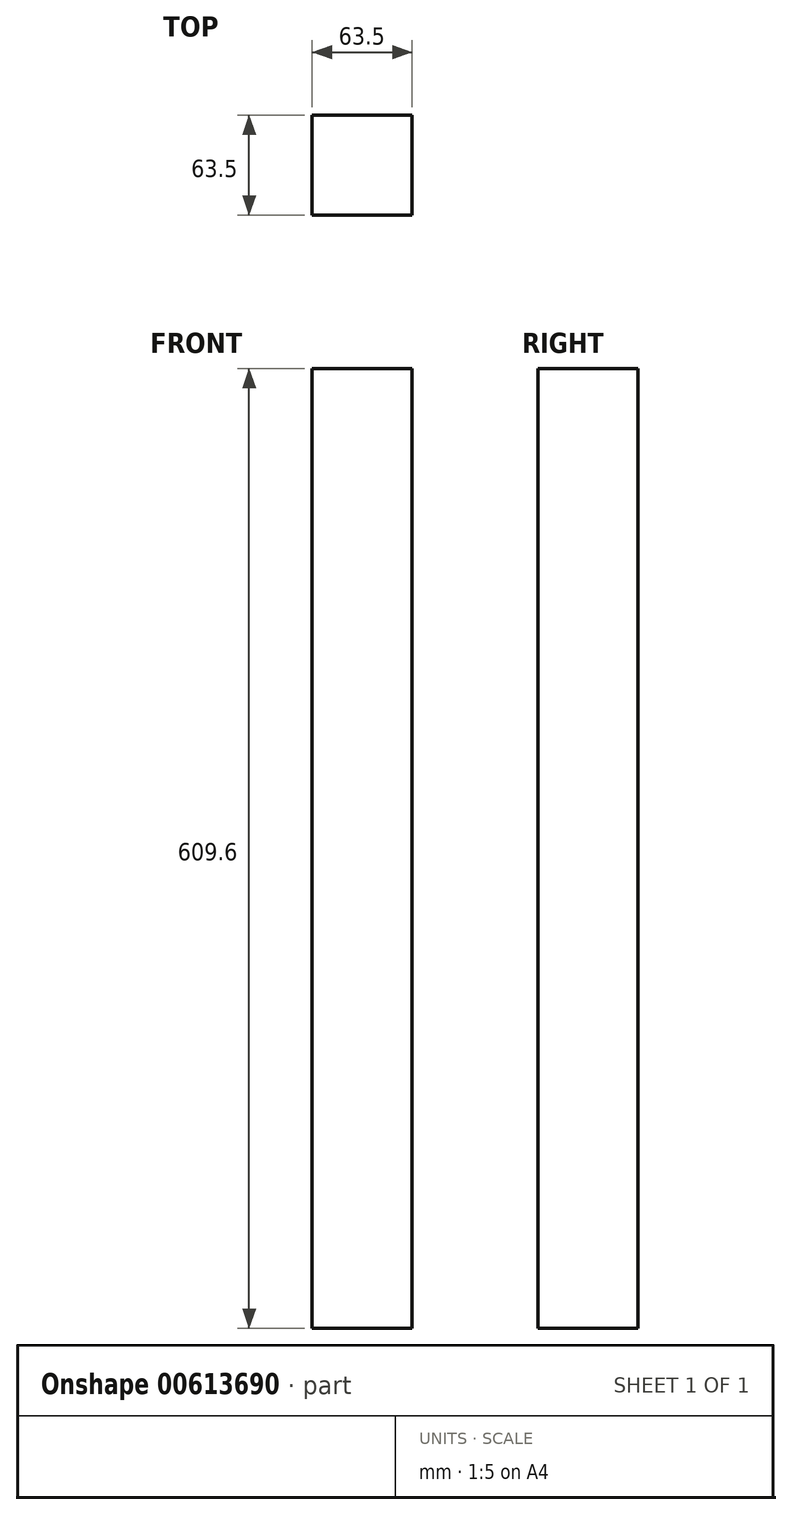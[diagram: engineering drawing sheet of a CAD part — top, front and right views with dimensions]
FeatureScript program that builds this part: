
annotation { "Feature Type Name" : "Feature", "Feature Type Description" : "" }
export const myFeature = defineFeature(function(context is Context, id is Id, definition is map)
    precondition{}
    {
        {
            var Q0;
            Q0=qCreatedBy(makeId("Front.planeOp"),FACE);
            var sketch = newSketch(context, id + "F0", { "sketchPlane" : qUnion([Q0])});
            skLineSegment(sketch, "E0.bottom", {"start": v(-89.6, 310.83) * mm, "end": v(-26.1, 310.83) * mm});
            skLineSegment(sketch, "E0.top", {"start": v(-89.6, -298.77) * mm, "end": v(-26.1, -298.77) * mm});
            skLineSegment(sketch, "E0.left", {"start": v(-89.6, 310.83) * mm, "end": v(-89.6, -298.77) * mm});
            skLineSegment(sketch, "E0.right", {"start": v(-26.1, 310.83) * mm, "end": v(-26.1, -298.77) * mm});
            skSolve(sketch);
        }
        {
            var Q0;
            Q0 = qSketchRegion(id + "F0", true);
            extrude(context, id + "F1", {"entities" : qUnion([Q0]), "depth" : 63.5 * mm, "offsetDistance" : 25.4 * mm});
        }
    });
